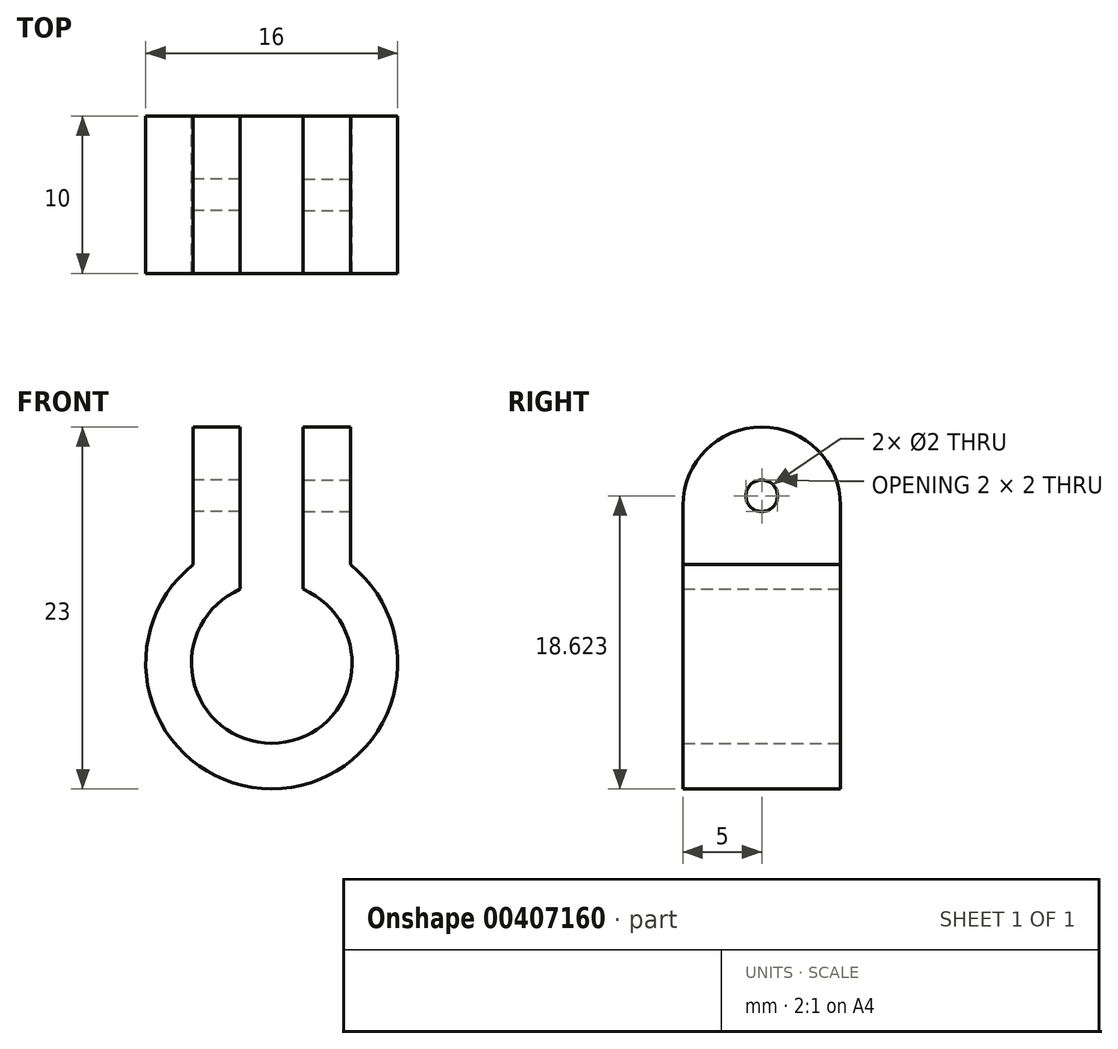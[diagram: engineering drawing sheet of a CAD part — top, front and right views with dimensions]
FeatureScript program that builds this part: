
annotation { "Feature Type Name" : "Feature", "Feature Type Description" : "" }
export const myFeature = defineFeature(function(context is Context, id is Id, definition is map)
    precondition{}
    {
        {
            var Q0;
            Q0=qCreatedBy(makeId("Front.planeOp"),FACE);
            var sketch = newSketch(context, id + "F0", { "sketchPlane" : qUnion([Q0])});
            skArc(sketch, "E0", {"start": v(0, -5.1) * mm, "mid": v(5, -1.02) * mm, "end": v(2, 4.7) * mm});
            skLineSegment(sketch, "E1", {"start": v(0, 0) * mm, "end": v(7.37, -3.12) * mm, "construction": true});
            skLineSegment(sketch, "E2", {"start": v(5, 15) * mm, "end": v(5, 6.24) * mm});
            skLineSegment(sketch, "E3", {"start": v(2, 4.7) * mm, "end": v(2, 15) * mm});
            skLineSegment(sketch, "E4.trimOffspring", {"start": v(2, 15) * mm, "end": v(5, 15) * mm});
            skLineSegment(sketch, "E5", {"start": v(0, 15) * mm, "end": v(0, -19.29) * mm, "construction": true});
            skArc(sketch, "E6.trimOffspring", {"start": v(0, -8) * mm, "mid": v(7.94, -1) * mm, "end": v(2, 7.75) * mm});
            skLineSegment(sketch, "E7", {"start": v(0, -5.1) * mm, "end": v(0, -8) * mm});
            skSolve(sketch);
        }
        {
            var Q0;
            {var subQ4=sQuery(id+"F0.wireOp",EDGE,"E3");var subQ6=sQuery(id+"F0.wireOp",EDGE,"E0");var subQ8=makeQuery(id+"F0.imprint","INTERSECT",VERTEX,{"derivedFrom":[subQ6,subQ4]});Q0=makeQuery(id+"F0.imprint","IMPRINT",FACE,{"disambiguationData":[TD([[makeQuery(id+"F0.imprint","IMPRINT",EDGE,{"disambiguationData":[TD([[subQ8,1.0]])],"derivedFrom":subQ6}),-1.0]])]});}
            var Q1;
            {var subQ0=sQuery(id+"F0.wireOp",EDGE,"HN6I2qcI-bxlO-N13F-bBn6-prmU2gU4knM3");var subQ1=sQuery(id+"F0.wireOp",EDGE,"E0");var subQ2=makeQuery(id+"F0.imprint","INTERSECT",VERTEX,{"derivedFrom":[subQ1,subQ0]});Q1=makeQuery(id+"F0.imprint","IMPRINT",FACE,{"disambiguationData":[TD([[makeQuery(id+"F0.imprint","IMPRINT",EDGE,{"disambiguationData":[TD([[subQ2,-1.0]])],"derivedFrom":subQ1}),-1.0]])]});}
            var Q2;
            {var subQ4=sQuery(id+"F0.wireOp",EDGE,"i9qYtkfv-SZLV-WTxb-UqVO-jSNCvkcmy04q");var subQ6=sQuery(id+"F0.wireOp",EDGE,"E0");var subQ8=makeQuery(id+"F0.imprint","INTERSECT",VERTEX,{"derivedFrom":[subQ6,subQ4]});Q2=makeQuery(id+"F0.imprint","IMPRINT",FACE,{"disambiguationData":[TD([[makeQuery(id+"F0.imprint","IMPRINT",EDGE,{"disambiguationData":[TD([[subQ8,-1.0]])],"derivedFrom":subQ6}),-1.0]])]});}
            var Q3;
            {var subQ3=sQuery(id+"F0.wireOp",EDGE,"g51z1Yhh-3KAa-QBzB-FuLV-YnATeuSFtZAR");Q3=makeQuery(id+"F0.imprint","IMPRINT",FACE,{"disambiguationData":[TD([[makeQuery(id+"F0.imprint","IMPRINT",EDGE,{"derivedFrom":subQ3}),-1.0]])]});}
            var Q4;
            {var subQ3=sQuery(id+"F0.wireOp",EDGE,"E2");Q4=makeQuery(id+"F0.imprint","IMPRINT",FACE,{"disambiguationData":[TD([[makeQuery(id+"F0.imprint","IMPRINT",EDGE,{"derivedFrom":subQ3}),-1.0]])]});}
            var Q5;
            {var subQ0=sQuery(id+"F0.wireOp",EDGE,"TJ68d5Vw-Muim-NUw3-UtEN-SQeXiUApDPQv");Q5=makeQuery(id+"F0.imprint","IMPRINT",FACE,{"disambiguationData":[TD([[makeQuery(id+"F0.imprint","IMPRINT",EDGE,{"derivedFrom":subQ0}),1.0]])]});}
            extrude(context, id + "F1", {"entities" : qUnion([Q0, Q1, Q2, Q3, Q4, Q5]), "endBound" : BoundingType.SYMMETRIC, "depth" : 10 * mm});
        }
        {
            var Q0;
            Q0=makeQuery(id+"F1.opExtrude","SWEPT_FACE",FACE,{"disambiguationData":[OSD([sQuery(id+"F0.wireOp",EDGE,"E2")])]});
            var sketch = newSketch(context, id + "F2", { "sketchPlane" : qUnion([Q0])});
            skLineSegment(sketch, "E8", {"start": v(-5, 10.62) * mm, "end": v(5, 10.62) * mm, "construction": true});
            skLineSegment(sketch, "E9", {"start": v(0, 15) * mm, "end": v(0, 6.24) * mm, "construction": true});
            skCircle(sketch, "E10", {"center": v(0, 10.62) * mm, "radius": 1 * mm});
            skSolve(sketch);
        }
        {
            var Q0;
            Q0=qSketchRegion(id+"F2",true);
            extrude(context, id + "F3", {"entities" : qUnion([Q0]), "operationType" : NewBodyOperationType.REMOVE, "oppositeDirection" : true, "depth" : 25 * mm});
        }
        {
            var Q0;
            Q0=makeQuery(id+"F1.opExtrude","CAP_EDGE",EDGE,{"disambiguationData":[OSD([sQuery(id+"F0.wireOp",EDGE,"TJ68d5Vw-Muim-NUw3-UtEN-SQeXiUApDPQv")])],"isStart":true});
            var Q1;
            Q1=makeQuery(id+"F1.opExtrude","CAP_EDGE",EDGE,{"disambiguationData":[OSD([sQuery(id+"F0.wireOp",EDGE,"TJ68d5Vw-Muim-NUw3-UtEN-SQeXiUApDPQv")])],"isStart":false});
            var Q2;
            Q2=makeQuery(id+"F1.opExtrude","CAP_EDGE",EDGE,{"disambiguationData":[OSD([sQuery(id+"F0.wireOp",EDGE,"E4.trimOffspring")])],"isStart":false});
            var Q3;
            Q3=makeQuery(id+"F1.opExtrude","CAP_EDGE",EDGE,{"disambiguationData":[OSD([sQuery(id+"F0.wireOp",EDGE,"E4.trimOffspring")])],"isStart":true});
            fillet(context, id + "F4", {"entities" : qUnion([Q0, Q1, Q2, Q3]), "radius" : 5 * mm, "tangentPropagation" : true, "allowEdgeOverflow" : false});
        }
        {
            var Q0;
            Q0=makeQuery(id+"F1.opExtrude","SWEPT_BODY",BODY,{"disambiguationData":[OSD([sQuery(id+"F0.wireOp",EDGE,"E0"),sQuery(id+"F0.wireOp",EDGE,"HN6I2qcI-bxlO-N13F-bBn6-prmU2gU4knM3"),sQuery(id+"F0.wireOp",EDGE,"TJ68d5Vw-Muim-NUw3-UtEN-SQeXiUApDPQv"),sQuery(id+"F0.wireOp",EDGE,"PdTNQA07-Jj0j-6zGr-cceW-6MmfTXDWng1i"),sQuery(id+"F0.wireOp",EDGE,"E2"),sQuery(id+"F0.wireOp",EDGE,"E3"),sQuery(id+"F0.wireOp",EDGE,"E4.trimOffspring"),sQuery(id+"F0.wireOp",EDGE,"E6.trimOffspring"),sQuery(id+"F0.wireOp",EDGE,"E7")])]});
            var Q1;
            Q1=qCreatedBy(makeId("Right.planeOp"),FACE);
            mirror(context, id + "F5", {"operationType" : NewBodyOperationType.ADD, "entities" : qUnion([Q0]), "mirrorPlane" : qUnion([Q1])});
        }
    });
